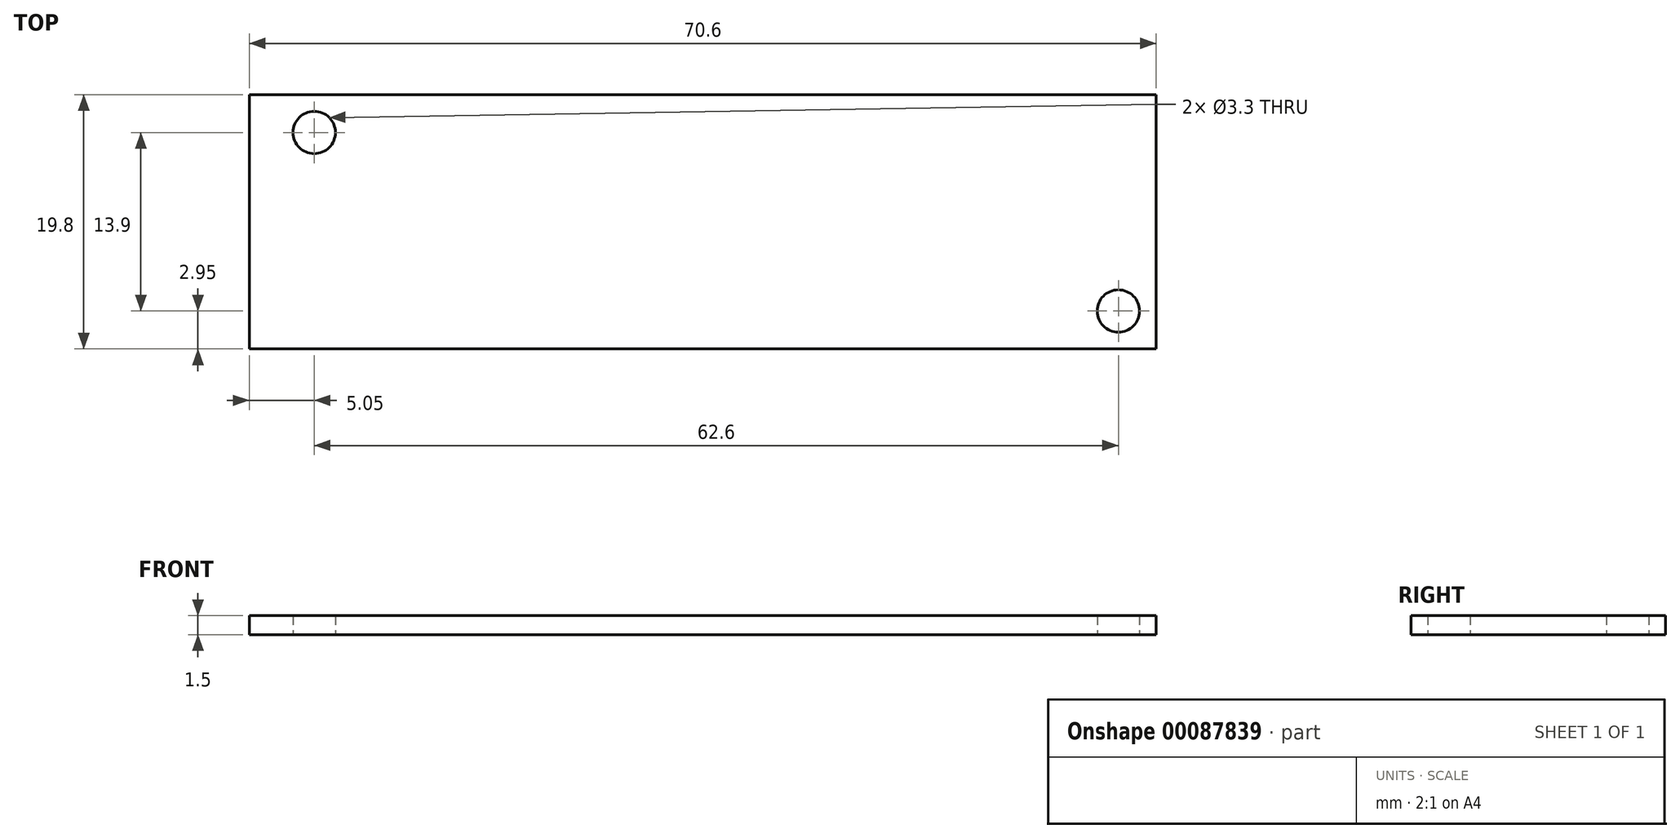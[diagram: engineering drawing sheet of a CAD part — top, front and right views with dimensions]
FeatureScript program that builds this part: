
annotation { "Feature Type Name" : "Feature", "Feature Type Description" : "" }
export const myFeature = defineFeature(function(context is Context, id is Id, definition is map)
    precondition{}
    {
        {
            var Q0;
            Q0=qCreatedBy(makeId("Top.planeOp"),FACE);
            var sketch = newSketch(context, id + "F0", { "sketchPlane" : qUnion([Q0])});
            skLineSegment(sketch, "E0.bottom", {"start": v(35.3, -9.9) * mm, "end": v(-35.3, -9.9) * mm});
            skLineSegment(sketch, "E0.top", {"start": v(35.3, 9.9) * mm, "end": v(-35.3, 9.9) * mm});
            skLineSegment(sketch, "E0.left", {"start": v(35.3, -9.9) * mm, "end": v(35.3, 9.9) * mm});
            skLineSegment(sketch, "E0.right", {"start": v(-35.3, -9.9) * mm, "end": v(-35.3, 9.9) * mm});
            skPoint(sketch, "E0.middle", {"position": v(0, 0) * mm});
            skCircle(sketch, "E1", {"center": v(-30.25, 6.95) * mm, "radius": 1.65 * mm});
            skCircle(sketch, "E2", {"center": v(32.35, -6.95) * mm, "radius": 1.65 * mm});
            skPoint(sketch, "E3", {"position": v(32.35, 6.95) * mm});
            skSolve(sketch);
        }
        {
            var Q0;
            Q0=makeQuery(id+"F0.imprint","IMPRINT",FACE,{"disambiguationData":[TD([[makeQuery(id+"F0.imprint","IMPRINT",EDGE,{"derivedFrom":sQuery(id+"F0.wireOp",EDGE,"E0.bottom")}),-1.0]])]});
            extrude(context, id + "F1", {"entities" : qUnion([Q0]), "depth" : 1.5 * mm});
        }
    });
